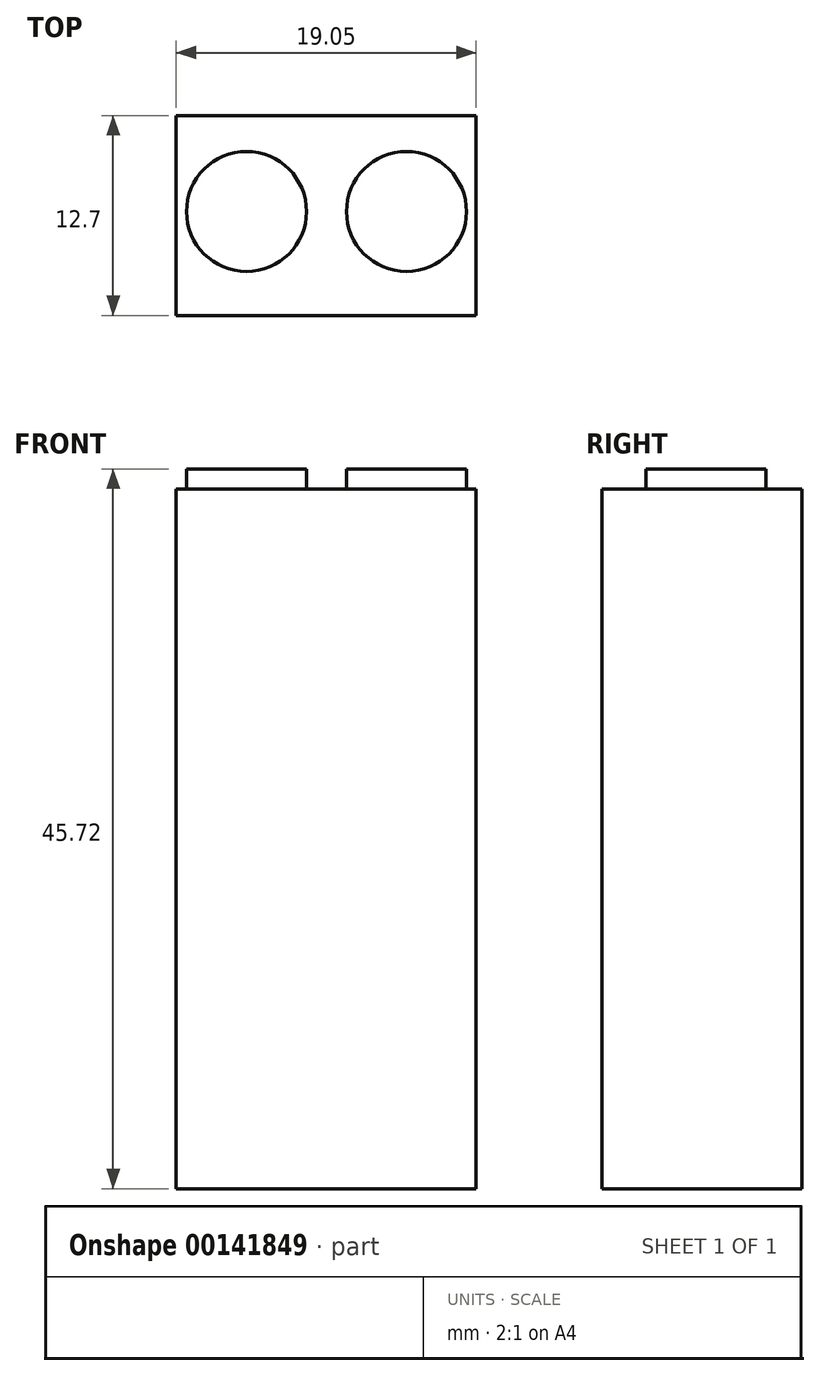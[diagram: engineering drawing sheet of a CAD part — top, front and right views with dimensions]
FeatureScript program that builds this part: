
annotation { "Feature Type Name" : "Feature", "Feature Type Description" : "" }
export const myFeature = defineFeature(function(context is Context, id is Id, definition is map)
    precondition{}
    {
        {
            var Q0;
            Q0=qCreatedBy(makeId("Front.planeOp"),FACE);
            var sketch = newSketch(context, id + "F0", { "sketchPlane" : qUnion([Q0])});
            skLineSegment(sketch, "E0.bottom", {"start": v(0, 0) * mm, "end": v(-19.05, 0) * mm});
            skLineSegment(sketch, "E0.top", {"start": v(0, -44.45) * mm, "end": v(-19.05, -44.45) * mm});
            skLineSegment(sketch, "E0.left", {"start": v(0, 0) * mm, "end": v(0, -44.45) * mm});
            skLineSegment(sketch, "E0.right", {"start": v(-19.05, 0) * mm, "end": v(-19.05, -44.45) * mm});
            skSolve(sketch);
        }
        {
            var Q0;
            Q0=makeQuery(id+"F0.imprint","IMPRINT",FACE,{"disambiguationData":[TD([[makeQuery(id+"F0.imprint","IMPRINT",EDGE,{"derivedFrom":sQuery(id+"F0.wireOp",EDGE,"E0.bottom")}),1.0]])]});
            extrude(context, id + "F1", {"entities" : qUnion([Q0]), "depth" : 12.7 * mm});
        }
        {
            var Q0;
            Q0=makeQuery(id+"F1.opExtrude","SWEPT_FACE",FACE,{"disambiguationData":[OSD([sQuery(id+"F0.wireOp",EDGE,"E0.bottom")])]});
            var sketch = newSketch(context, id + "F2", { "sketchPlane" : qUnion([Q0])});
            skCircle(sketch, "E1", {"center": v(-14.58, -6.1) * mm, "radius": 3.81 * mm});
            skCircle(sketch, "E2", {"center": v(-4.42, -6.1) * mm, "radius": 3.81 * mm});
            skSolve(sketch);
        }
        {
            var Q0;
            Q0 = qSketchRegion(id + "F2", true);
            extrude(context, id + "F3", {"entities" : qUnion([Q0]), "depth" : 1.27 * mm});
        }
    });
